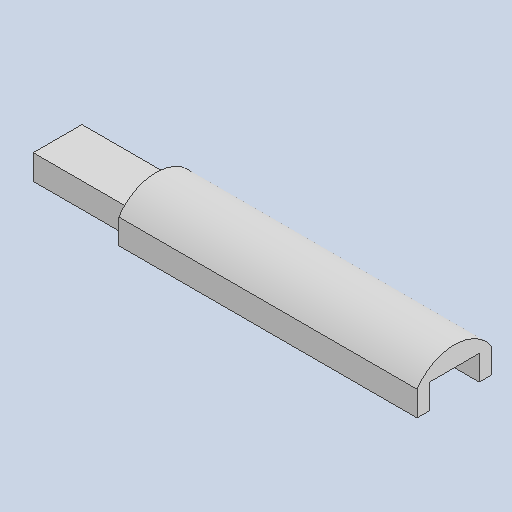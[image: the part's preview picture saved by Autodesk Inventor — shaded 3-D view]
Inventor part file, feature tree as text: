
AUTODESK INVENTOR PART (.ipt)
format: ipt  version: 2023 (Build 270158000, 158)  size: 264,192 bytes
history: native  units: in
note: dims shown in document units (in); Inventor stores cm internally (conversion verified against a paired STEP export)
features: extrude x3, sketch x3, projected_geometry x2
ambient origin geometry x8: Origin, YZ Plane, XZ Plane, XY Plane, X Axis, Y Axis, Z Axis, Center Point
bodies: Solid1 (feature_tree)
feature tree (8):
  extrude  "Extrusion1"  Depth=0.75in
  extrude  "Extrusion2"  Depth=1.5in
  extrude  "Extrusion3"  Depth=0.49in
  sketch  "Sketch1"  dims[d0=3.0in d1=0.75in]
  sketch  "Sketch2"  dims[d2=0.375in d3=1.5in]
  projected_geometry  "Projected Loop1"
  sketch  "Sketch3"  dims[d4=0.99in d5=0.49in d6=0.245in d7=0.25in d8=0.0in d9=3.0in d10=0.0in d11=0.5in d12=0.49in d13=0.25in d14=1.0in d15=0.25in d16=0.0in]
  projected_geometry  "Projected Loop2"
